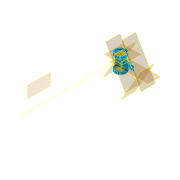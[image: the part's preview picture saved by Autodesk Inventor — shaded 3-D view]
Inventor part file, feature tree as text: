
AUTODESK INVENTOR PART (.ipt)
format: ipt  version: 2021 (Build 250183000, 183)  size: 385,536 bytes
history: native  units: in
note: dims shown in document units (in); Inventor stores cm internally (conversion verified against a paired STEP export)
features: sketch x16, extrude x11, plane x9, revolve x4, projected_geometry x3, fillet x2, pattern_circular x2, mirror x2
ambient origin geometry x8: Origin, YZ Plane, XZ Plane, XY Plane, X Axis, Y Axis, Z Axis, Center Point
bodies: Solid1 (feature_tree), Solid2 (feature_tree), Solid3 (feature_tree)
feature tree (49):
  extrude  "Extrusion1"  Depth=0.0787in
  revolve  "Revolution1"  Angle=90.0deg
  revolve  "Revolution2"  [1 undecoded]
  extrude  "Extrusion9"  Depth=0.0197in TaperAngle=0.0deg
  plane  "Work Plane6"
  plane  "Work Plane5"
  extrude  "Extrusion13"  Depth=0.2362in
  revolve  "Revolution3"  [1 undecoded]
  fillet  "Fillet3"  Radius=0.2362in
  pattern_circular  "Circular Pattern5"  [2 undecoded]
  plane  "Work Plane8"
  extrude  "Extrusion14"  TaperAngle=15.0deg  [1 undecoded]
  pattern_circular  "Circular Pattern6"  [2 undecoded]
  extrude  "Extrusion15"  Depth=0.0197in TaperAngle=360.0deg
  mirror  "Mirror3"
  extrude  "Extrusion11"  Depth=0.0197in
  fillet  "Fillet2"  Radius=0.315in
  extrude  "Extrusion20"  Depth=0.0197in
  plane  "Work Plane15"
  extrude  "Extrusion22"  Depth=0.3937in TaperAngle=0.0deg
  plane  "Work Plane10"
  plane  "Work Plane12"
  plane  "Work Plane14"
  sketch  "Sketch39"  dims[d97=0.0787in]
  extrude  "Extrusion25"  Depth=0.0197in TaperAngle=360.0deg
  extrude  "Extrusion26"  Depth=0.0394in
  revolve  "Revolution5"  [1 undecoded]
  extrude  "Extrusion27"  Depth=0.0197in
  mirror  "Mirror12"
  sketch  "Sketch2"  dims[d0=0.1575in d1=0.0787in]
  sketch  "Sketch3"  dims[d2=0.0787in d3=0.0in d9=90.0deg]
  sketch  "Sketch4"  dims[d15=90.0deg d71=0.0984in d72=0.0in]
  sketch  "Sketch15"  dims[d73=0.1575in d74=0.0197in d75=0.0in]
  sketch  "Sketch19"  dims[d76=0.1875in d81=0.2362in]
  sketch  "Sketch21"  dims[d82=0.2756in d83=0.1181in d84=0.2362in]
  sketch  "Sketch23"  dims[d85=0.1181in]
  sketch  "Sketch26"  dims[d86=0.0in d87=0.0in]
  sketch  "Sketch27"  dims[d88=0.0687in]
  sketch  "Sketch34"  dims[d95=0.2542in]
  sketch  "Sketch36"  dims[d96=0.0315in]
  plane  "Work Plane11"
  plane  "Work Plane13"
  sketch  "Sketch41"  dims[d99=0.0984in]
  projected_geometry  "Projected Loop2"
  sketch  "Sketch43"  dims[d100=15.0deg]
  sketch  "Sketch44"  dims[d101=0.0374in]
  sketch  "Sketch45"  dims[d102=0.0906in d103=0.0in d105=0.0472in d106=15.0deg d107=0.0118in d108=1.5748in d109=360.0deg d114=0.1575in d115=0.315in d117=0.1181in d118=0.3937in d119=0.0in d122=0.7874in d123=360.0deg d125=0.0394in d126=0.0787in d127=0.0in d128=0.5118in d143=0.0515in d152=0.0591in d153=0.0in d160=0.0787in d161=0.0787in d162=0.0591in d163=0.0in d172=30.0deg d173=0.8543in d174=-0.2061in d175=0.9724in d178=0.0787in d181=0.0591in d182=0.3937in d183=0.0in d191=0.1024in d192=0.0512in d193=0.2756in d194=0.0in d195=0.063in d196=0.0394in d197=0.0709in d198=0.0551in d199=0.0866in d200=0.1378in d201=0.0709in d202=90.0deg d203=0.2756in d204=0.0in d19=0.0197in d20=0.0344in d21=0.0197in d22=0.0344in d116=0.0197in d133=0.0197in d134=0.0344in d135=0.0197in d136=0.0344in d179=0.0197in d180=0.0344in]
  projected_geometry  "Project Cut Edges1"
  projected_geometry  "Project Cut Edges3"
note: 8 required parameter values undecoded (feature->parameter linkage not recoverable at this tier; creation-order binding heuristic only, values carry confidence <= 0.55)